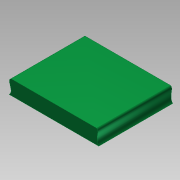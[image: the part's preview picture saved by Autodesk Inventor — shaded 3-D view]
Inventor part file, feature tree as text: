
AUTODESK INVENTOR PART (.ipt)
format: ipt  version: 2011 (Build 150239000, 239)  size: 86,528 bytes
history: native  units: mm
features: extrude x2, sketch x2, other x1
ambient origin geometry x8: Origin, YZ Plane, XZ Plane, XY Plane, X Axis, Y Axis, Z Axis, Center Point
feature tree (5):
  other  "Твердое тело1"
  extrude  "Выдавливание1"  Depth=1.5mm TaperAngle=0.0deg
  extrude  "Выдавливание2"  Depth=1.5mm TaperAngle=0.0deg
  sketch  "Эскиз1"
  sketch  "Эскиз2"
